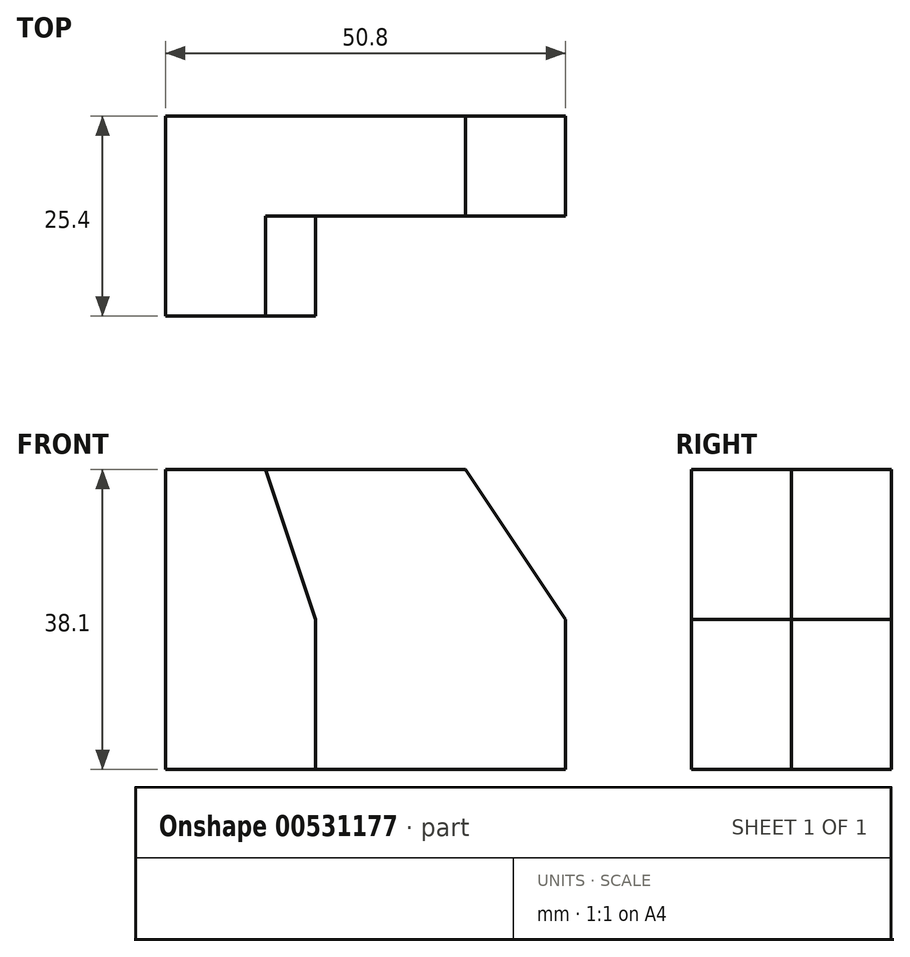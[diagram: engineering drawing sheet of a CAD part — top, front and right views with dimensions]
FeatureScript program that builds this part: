
annotation { "Feature Type Name" : "Feature", "Feature Type Description" : "" }
export const myFeature = defineFeature(function(context is Context, id is Id, definition is map)
    precondition{}
    {
        {
            var Q0;
            Q0=qCreatedBy(makeId("Top.planeOp"),FACE);
            var sketch = newSketch(context, id + "F0", { "sketchPlane" : qUnion([Q0])});
            skLineSegment(sketch, "E0", {"start": v(0, 0) * mm, "end": v(0, -25.4) * mm});
            skLineSegment(sketch, "E1", {"start": v(0, -25.4) * mm, "end": v(12.7, -25.4) * mm});
            skLineSegment(sketch, "E2", {"start": v(12.7, -25.4) * mm, "end": v(12.7, -12.7) * mm});
            skLineSegment(sketch, "E3", {"start": v(0, 0) * mm, "end": v(38.1, 0) * mm});
            skLineSegment(sketch, "E4", {"start": v(38.1, 0) * mm, "end": v(38.1, -12.7) * mm});
            skLineSegment(sketch, "E5", {"start": v(38.1, -12.7) * mm, "end": v(12.7, -12.7) * mm});
            skPoint(sketch, "E6.start.orphan", {"position": v(0, -12.7) * mm});
            skSolve(sketch);
        }
        {
            var Q0;
            Q0=qCreatedBy(makeId("Top.planeOp"),FACE);
            cPlane(context, id + "F1", {"entities" : qUnion([Q0]), "cplaneType" : CPlaneType.OFFSET, "offset" : 38.1 * mm, "oppositeDirection" : true, "width" : 152.4 * mm, "height" : 152.4 * mm});
        }
        {
            var Q0;
            Q0=qCreatedBy(makeId("Top.planeOp"),FACE);
            cPlane(context, id + "F2", {"entities" : qUnion([Q0]), "cplaneType" : CPlaneType.OFFSET, "offset" : 19.05 * mm, "oppositeDirection" : true, "width" : 152.4 * mm, "height" : 152.4 * mm});
        }
        {
            var Q0;
            Q0=qCreatedBy(id+"F2.planeOp",FACE);
            var sketch = newSketch(context, id + "F3", { "sketchPlane" : qUnion([Q0])});
            skLineSegment(sketch, "E7", {"start": v(0, 0) * mm, "end": v(50.8, 0) * mm});
            skLineSegment(sketch, "E8", {"start": v(50.8, 0) * mm, "end": v(50.8, -12.7) * mm});
            skLineSegment(sketch, "E9", {"start": v(50.8, -12.7) * mm, "end": v(19.05, -12.7) * mm});
            skLineSegment(sketch, "E10", {"start": v(19.05, -12.7) * mm, "end": v(19.05, -25.4) * mm});
            skLineSegment(sketch, "E11", {"start": v(19.05, -25.4) * mm, "end": v(0, -25.4) * mm});
            skLineSegment(sketch, "E12", {"start": v(0, -25.4) * mm, "end": v(0, 0) * mm});
            skSolve(sketch);
        }
        {
            var Q0;
            Q0=makeQuery(id+"F3.imprint","IMPRINT",FACE,{"disambiguationData":[TD([[makeQuery(id+"F3.imprint","IMPRINT",EDGE,{"derivedFrom":sQuery(id+"F3.wireOp",EDGE,"E7")}),-1.0]])]});
            extrude(context, id + "F4", {"entities" : qUnion([Q0]), "oppositeDirection" : true, "depth" : 19.05 * mm, "offsetDistance" : 25.4 * mm});
        }
        {
            var Q1;
            Q1=makeQuery(id+"F0.imprint","IMPRINT",FACE,{"disambiguationData":[TD([[makeQuery(id+"F0.imprint","IMPRINT",EDGE,{"derivedFrom":sQuery(id+"F0.wireOp",EDGE,"E0")}),1.0]])]});
            var Q2;
            Q2=makeQuery(id+"F4.opExtrude","CAP_FACE",FACE,{"disambiguationData":[OSD([sQuery(id+"F3.wireOp",EDGE,"E7"),sQuery(id+"F3.wireOp",EDGE,"E8"),sQuery(id+"F3.wireOp",EDGE,"E9"),sQuery(id+"F3.wireOp",EDGE,"E10"),sQuery(id+"F3.wireOp",EDGE,"E11"),sQuery(id+"F3.wireOp",EDGE,"E12")])],"isStart":true});
            loft(context, id + "F5", {"operationType" : NewBodyOperationType.ADD, "sheetProfilesArray" : [{ "sheetProfileEntities" : qUnion([Q1]) }, { "sheetProfileEntities" : qUnion([Q2]) }]});
        }
    });
